# Revit family: Accessory-Step_Can-KOHLER-Eolia-K-17531T_1
name_source: partatom
category: Specialty Equipment
units: mm (PartAtom-declared; Revit-internal decimal feet)

## family parameters
Cut with Voids When Loaded = No
Host = Face
OmniClass Number = 23.31.25.00
OmniClass Title = Toilet and Bath Specialties
Part Type = Normal
Room Calculation Point = No
Round Connector Dimension = Use Diameter
Shared = No

## types (1)
- ST-Stainless Steel
    ADA Compliant = No
    Assembly Code = C1030200
    Date Modified = 11/08/2022
    Default Elevation = 0"
    Description = Pedal Trash Can
    Finish = KOHLER-Metal-ST-Stainless_Steel
    Height = 12 3/8"
    Length = 13 1/2"
    Manufacturer = Kohler Co.
    Master Format 2014 = 10 28 00
    Master Format 2014 Name = Toilet, Bath, and Laundry Accessories
    Material = Stainless Steel Construction
    Model = K-17531T-ST
    Product Documentation Link = https://files.kohler.com.cn
    Product Name = Eolia
    Product Page URL = https://www.kohler.com.cn
    Type = 1
    URL = http://www.kohler.com.cn
    WaterSense Certified = No
    Width = 8 1/4"

## geometry (parser evidence)
native form markers: Sweep x5
no freeform markers — native parametric forms only
